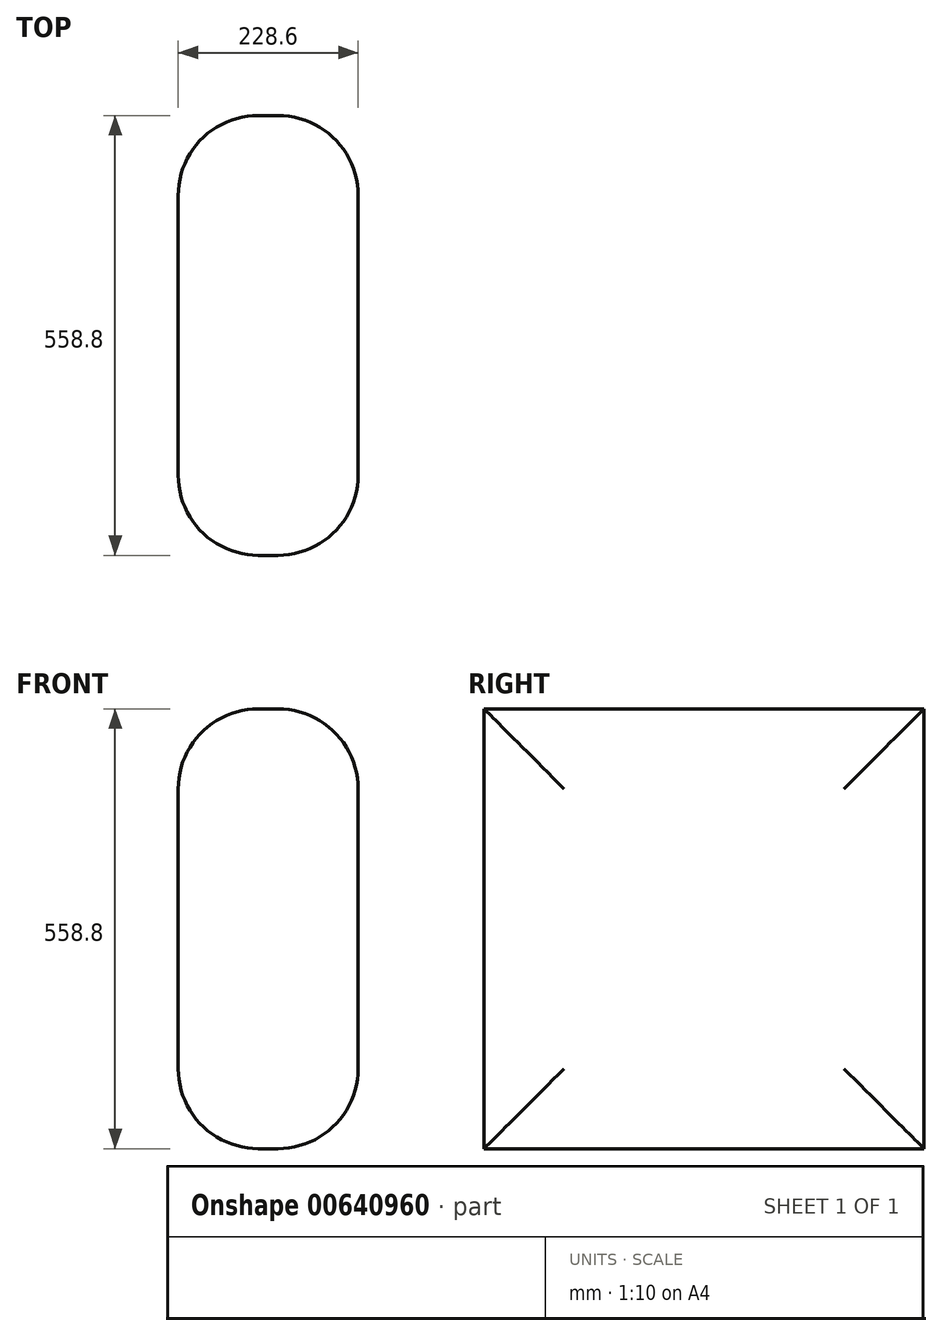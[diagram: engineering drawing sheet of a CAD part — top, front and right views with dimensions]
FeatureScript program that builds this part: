
annotation { "Feature Type Name" : "Feature", "Feature Type Description" : "" }
export const myFeature = defineFeature(function(context is Context, id is Id, definition is map)
    precondition{}
    {
        {
            var Q0;
            Q0=qCreatedBy(makeId("Top.planeOp"),FACE);
            var sketch = newSketch(context, id + "F0", { "sketchPlane" : qUnion([Q0])});
            skLineSegment(sketch, "E0.bottom", {"start": v(-253.01, 515.56) * mm, "end": v(-24.41, 515.56) * mm});
            skLineSegment(sketch, "E0.top", {"start": v(-253.01, -43.24) * mm, "end": v(-24.41, -43.24) * mm});
            skLineSegment(sketch, "E0.left", {"start": v(-253.01, 515.56) * mm, "end": v(-253.01, -43.24) * mm});
            skLineSegment(sketch, "E0.right", {"start": v(-24.41, 515.56) * mm, "end": v(-24.41, -43.24) * mm});
            skSolve(sketch);
        }
        {
            var Q0;
            Q0=qSketchRegion(id+"F0",true);
            extrude(context, id + "F1", {"entities" : qUnion([Q0]), "depth" : 558.8 * mm});
        }
        {
            var Q0;
            Q0=makeQuery(id+"F1.opExtrude","SWEPT_FACE",FACE,{"disambiguationData":[OSD([sQuery(id+"F0.wireOp",EDGE,"E0.right")])]});
            var Q1;
            Q1=makeQuery(id+"F1.opExtrude","SWEPT_FACE",FACE,{"disambiguationData":[OSD([sQuery(id+"F0.wireOp",EDGE,"E0.left")])]});
            fillet(context, id + "F2", {"entities" : qUnion([Q0, Q1]), "radius" : 101.6 * mm, "tangentPropagation" : true, "allowEdgeOverflow" : false});
        }
    });
